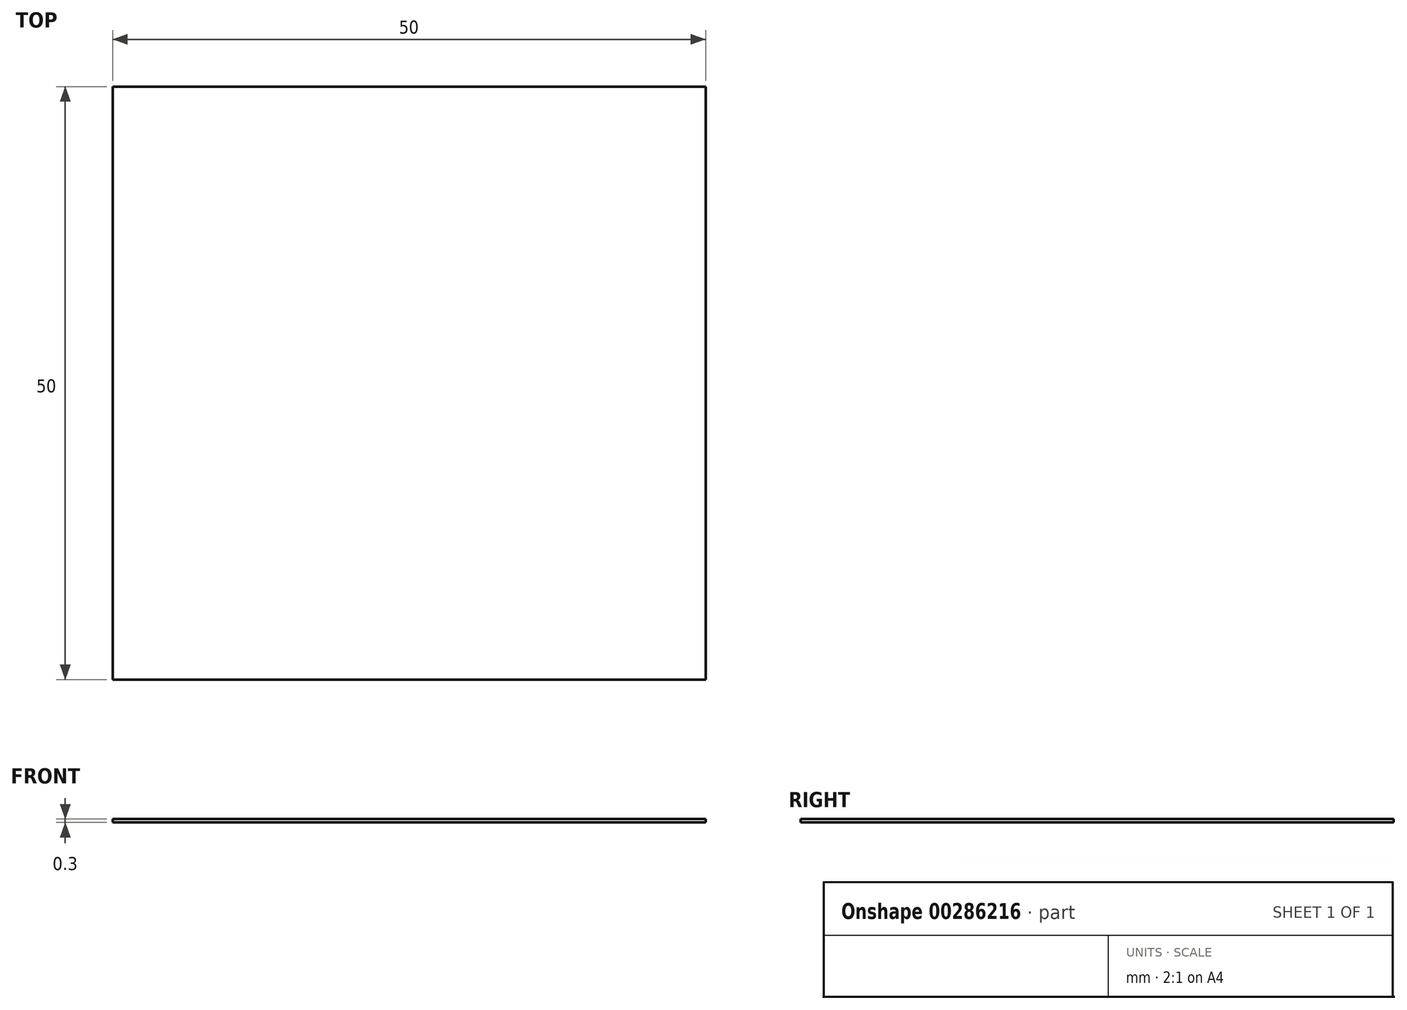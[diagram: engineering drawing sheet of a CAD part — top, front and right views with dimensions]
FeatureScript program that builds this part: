
annotation { "Feature Type Name" : "Feature", "Feature Type Description" : "" }
export const myFeature = defineFeature(function(context is Context, id is Id, definition is map)
    precondition{}
    {
        {
            var Q0;
            Q0=qCreatedBy(makeId("Top.planeOp"),FACE);
            var sketch = newSketch(context, id + "F0", { "sketchPlane" : qUnion([Q0])});
            skPoint(sketch, "E0.middle", {"position": v(0, 0) * mm});
            skLineSegment(sketch, "E1.bottom", {"start": v(25, -25) * mm, "end": v(-25, -25) * mm});
            skLineSegment(sketch, "E1.top", {"start": v(25, 25) * mm, "end": v(-25, 25) * mm});
            skLineSegment(sketch, "E1.left", {"start": v(25, -25) * mm, "end": v(25, 25) * mm});
            skLineSegment(sketch, "E1.right", {"start": v(-25, -25) * mm, "end": v(-25, 25) * mm});
            skSolve(sketch);
        }
        {
            var Q0;
            Q0 = qSketchRegion(id + "F0", true);
            extrude(context, id + "F1", {"entities" : qUnion([Q0]), "depth" : 0.3 * mm});
        }
    });
